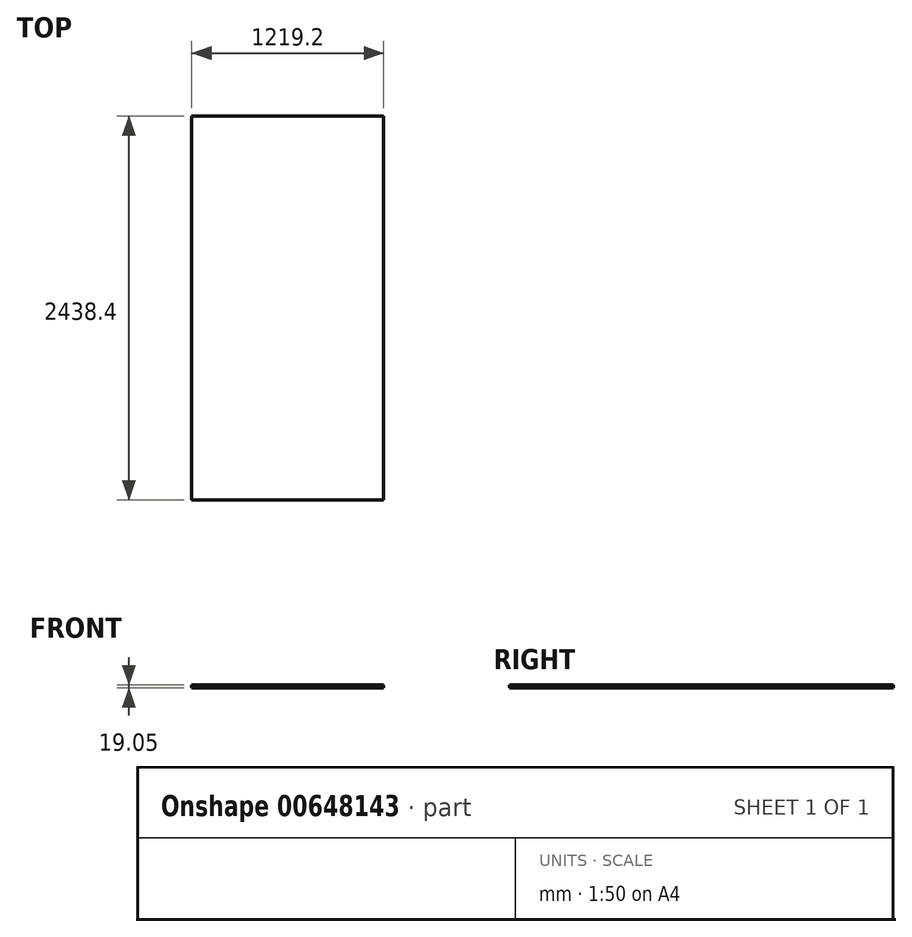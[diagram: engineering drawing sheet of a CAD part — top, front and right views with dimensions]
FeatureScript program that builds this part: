
annotation { "Feature Type Name" : "Feature", "Feature Type Description" : "" }
export const myFeature = defineFeature(function(context is Context, id is Id, definition is map)
    precondition{}
    {
        {
            var Q0;
            Q0=qCreatedBy(makeId("Top.planeOp"),FACE);
            var sketch = newSketch(context, id + "F0", { "sketchPlane" : qUnion([Q0])});
            skLineSegment(sketch, "E0.bottom", {"start": v(0, 0) * mm, "end": v(-1219.2, 0) * mm});
            skLineSegment(sketch, "E0.top", {"start": v(0, 2438.4) * mm, "end": v(-1219.2, 2438.4) * mm});
            skLineSegment(sketch, "E0.left", {"start": v(0, 0) * mm, "end": v(0, 2438.4) * mm});
            skLineSegment(sketch, "E0.right", {"start": v(-1219.2, 0) * mm, "end": v(-1219.2, 2438.4) * mm});
            skSolve(sketch);
        }
        {
            var Q0;
            Q0 = qSketchRegion(id + "F0", true);
            extrude(context, id + "F1", {"entities" : qUnion([Q0]), "depth" : 19.05 * mm, "offsetDistance" : 25.4 * mm});
        }
    });
